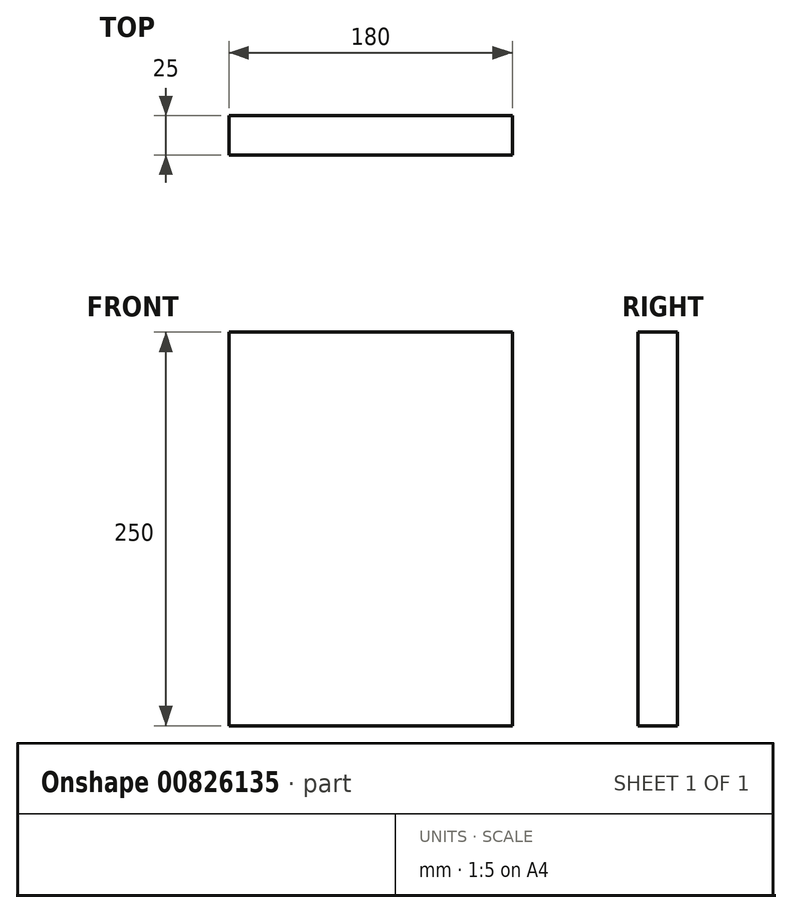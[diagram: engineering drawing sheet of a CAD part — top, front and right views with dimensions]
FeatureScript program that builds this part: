
annotation { "Feature Type Name" : "Feature", "Feature Type Description" : "" }
export const myFeature = defineFeature(function(context is Context, id is Id, definition is map)
    precondition{}
    {
        {
            var Q0;
            Q0=qCreatedBy(makeId("Front.planeOp"),FACE);
            var sketch = newSketch(context, id + "F0", { "sketchPlane" : qUnion([Q0])});
            skLineSegment(sketch, "E0.bottom", {"start": v(60, -110.84) * mm, "end": v(-120, -110.84) * mm});
            skLineSegment(sketch, "E0.top", {"start": v(60, 139.16) * mm, "end": v(-120, 139.16) * mm});
            skLineSegment(sketch, "E0.left", {"start": v(60, -110.84) * mm, "end": v(60, 139.16) * mm});
            skLineSegment(sketch, "E0.right", {"start": v(-120, -110.84) * mm, "end": v(-120, 139.16) * mm});
            skLineSegment(sketch, "E1", {"start": v(-84, -110.84) * mm, "end": v(-84, 139.16) * mm});
            skLineSegment(sketch, "E2", {"start": v(-48, 139.16) * mm, "end": v(-48, -110.84) * mm});
            skLineSegment(sketch, "E3", {"start": v(-12, -110.84) * mm, "end": v(-12, 139.16) * mm});
            skPoint(sketch, "E4.end.orphan", {"position": v(-30, 139.16) * mm});
            skPoint(sketch, "E4.start.orphan", {"position": v(-30, -110.84) * mm});
            skPoint(sketch, "E5.start.orphan", {"position": v(0, -110.84) * mm});
            skLineSegment(sketch, "E6", {"start": v(24, 139.16) * mm, "end": v(24, -110.84) * mm});
            skSolve(sketch);
        }
        {
            var Q0;
            Q0 = qSketchRegion(id + "F0", true);
            extrude(context, id + "F1", {"entities" : qUnion([Q0]), "depth" : 25 * mm, "offsetDistance" : 25 * mm});
        }
    });
